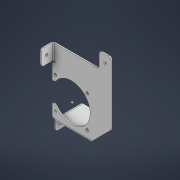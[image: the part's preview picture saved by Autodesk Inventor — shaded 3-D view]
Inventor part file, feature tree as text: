
AUTODESK INVENTOR PART (.ipt)
format: ipt  version: 2022 (Build 260153000, 153)  size: 249,344 bytes
history: native  units: mm
features: other x12, sheet_metal_op x8, reference x7, sketch x6, chamfer x3, hole x2
ambient origin geometry x8: Origin, YZ Plane, XZ Plane, XY Plane, X Axis, Y Axis, Z Axis, Center Point
bodies: Solid1 (feature_tree)
feature tree (38):
  sheet_metal_op  "Face1"
  sheet_metal_op  "Face2"
  sheet_metal_op  "Face3"
  sheet_metal_op  "Flange1"
  hole  "Hole1"  [1 undecoded]
  hole  "Hole2"  [1 undecoded]
  chamfer  "Corner Round1"
  chamfer  "Corner Round2"
  chamfer  "Corner Round3"
  other  "Corner Chamfer1"
  sketch  "Sketch1"  dims[d6=3.0mm d9=45.0deg]
  reference  "Reference3"
  reference  "Reference4"
  other  "Plate1"
  reference  "Reference5"
  reference  "Reference6"
  reference  "Reference7"
  reference  "Reference8"
  reference  "Reference9"
  sketch  "Sketch3"  dims[d10=210.0mm d11=30.0mm]
  other  "Plate2"
  sheet_metal_op  "Bend1"
  sketch  "Sketch4"  dims[d13=96.0mm]
  other  "Plate3"
  sheet_metal_op  "Bend2"
  sketch  "Sketch5"  dims[d18=40.0mm]
  other  "Plate4"
  sheet_metal_op  "Bend3"
  sheet_metal_op  "Corner1"
  sketch  "Sketch6"  dims[d19=40.0mm]
  sketch  "Sketch7"  dims[d20=30.0mm d21=3.0mm d22=3.0mm d23=1.5mm d24=6.0mm d25=3.0mm d26=45.0deg d27=70.0mm d28=3.0mm d29=3.0mm d30=1.5mm d31=6.0mm d32=3.0mm d33=3.0mm d34=1.5mm d35=6.0mm d36=3.0mm d37=30.0mm d38=90.0deg d39=3.0mm d40=12.0mm d41=3.0mm d42=3.0mm d43=50.0mm d44=6.6mm d45=6.0mm d46=12.6mm d47=2.0mm d48=90.0deg d49=3.0mm d50=20.594885mm d51=50.0mm d52=40.0mm d53=6.6mm d54=6.0mm d55=4.0mm d56=2.0mm d57=90.0deg d58=8.0mm d59=20.594885mm d60=6.0mm d61=6.0mm d62=2.0mm d63=4.0mm d64=6.0mm d65=45.0deg d66=120.0mm d67=100.0mm]
  other  "RobotPallet.iam"
  other  "EstructuraInferior:1"
  other  "Frame_Base:1"
  other  "ISO 10799-2 40x40x2 - 437.5:2"
  other  "ISO 10799-2 40x40x2 - 2899.41:1"
  other  "BL Motor + Encoder + Gearbox + Rueda:2"
  other  "bg-95x80-885950205312:1"
note: 2 required parameter values undecoded (feature->parameter linkage not recoverable at this tier; creation-order binding heuristic only, values carry confidence <= 0.55)
